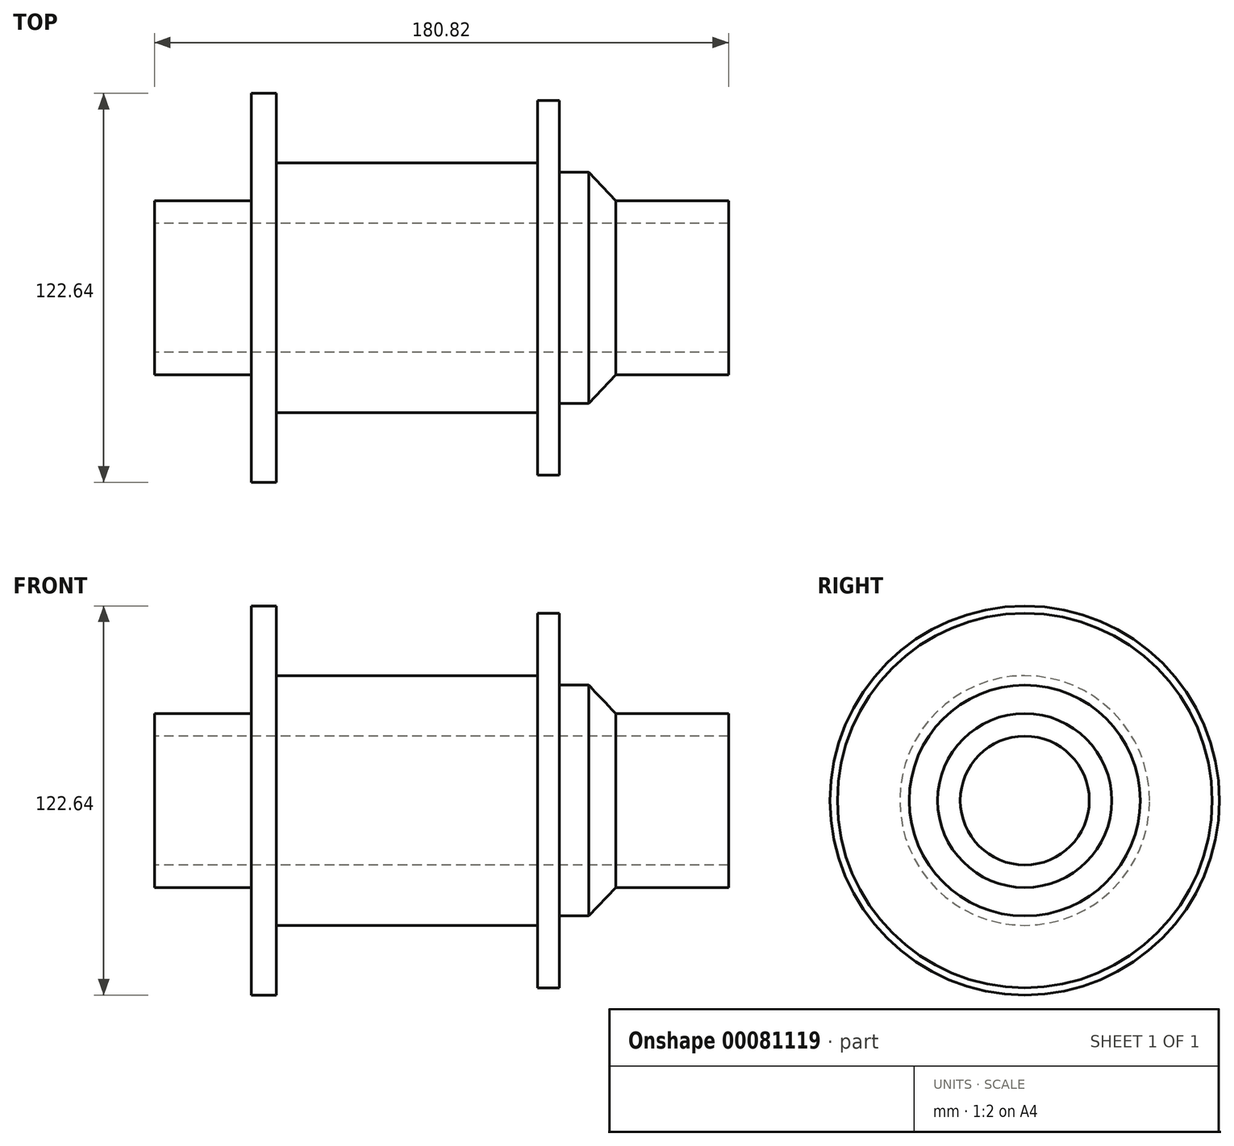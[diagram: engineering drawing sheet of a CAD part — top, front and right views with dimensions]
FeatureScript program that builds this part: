
annotation { "Feature Type Name" : "Feature", "Feature Type Description" : "" }
export const myFeature = defineFeature(function(context is Context, id is Id, definition is map)
    precondition{}
    {
        {
            var Q0;
            Q0=qCreatedBy(makeId("Front.planeOp"),FACE);
            var sketch = newSketch(context, id + "F0", { "sketchPlane" : qUnion([Q0])});
            skLineSegment(sketch, "E0.bottom", {"start": v(-90.41, 27.43) * mm, "end": v(90.41, 27.43) * mm});
            skLineSegment(sketch, "E0.top", {"start": v(-90.41, 20.32) * mm, "end": v(90.41, 20.32) * mm});
            skLineSegment(sketch, "E0.left", {"start": v(-90.41, 27.43) * mm, "end": v(-90.41, 20.32) * mm});
            skLineSegment(sketch, "E0.right", {"start": v(90.41, 27.43) * mm, "end": v(90.41, 20.32) * mm});
            skPoint(sketch, "E0.middle", {"position": v(0, 23.87) * mm});
            skLineSegment(sketch, "E1", {"start": v(-89.9, 0) * mm, "end": v(98.54, 0) * mm, "construction": true});
            skLineSegment(sketch, "E2", {"start": v(-59.88, 27.43) * mm, "end": v(-59.88, 61.32) * mm});
            skLineSegment(sketch, "E3", {"start": v(-59.88, 61.32) * mm, "end": v(-52, 61.32) * mm});
            skLineSegment(sketch, "E4", {"start": v(-52, 61.32) * mm, "end": v(-52, 39.35) * mm});
            skLineSegment(sketch, "E5", {"start": v(-52, 39.35) * mm, "end": v(30.3, 39.35) * mm});
            skLineSegment(sketch, "E6", {"start": v(30.3, 39.35) * mm, "end": v(30.3, 59.02) * mm});
            skLineSegment(sketch, "E7", {"start": v(30.3, 59.02) * mm, "end": v(37.18, 59.02) * mm});
            skLineSegment(sketch, "E8", {"start": v(37.18, 59.02) * mm, "end": v(37.18, 36.4) * mm});
            skLineSegment(sketch, "E9", {"start": v(37.18, 36.4) * mm, "end": v(46.36, 36.4) * mm});
            skLineSegment(sketch, "E10", {"start": v(46.36, 36.4) * mm, "end": v(54.89, 27.43) * mm});
            skSolve(sketch);
        }
        {
            var Q0;
            Q0 = qSketchRegion(id + "F0", true);
            var Q1;
            Q1=sQuery(id+"F0.wireOp",EDGE,"E1");
            revolve(context, id + "F1", {"entities" : qUnion([Q0]), "axis" : qUnion([Q1]), "revolveType" : RevolveType.FULL});
        }
    });
